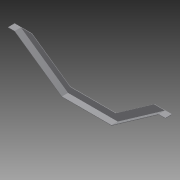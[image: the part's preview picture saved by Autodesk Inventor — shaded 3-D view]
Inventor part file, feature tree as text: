
AUTODESK INVENTOR PART (.ipt)
format: ipt  version: 2012 (Build 160160000, 160)  size: 97,280 bytes
history: native  units: in
note: dims shown in document units (in); Inventor stores cm internally (conversion verified against a paired STEP export)
features: extrude x2, sketch x1
ambient origin geometry x8: Origin, YZ Plane, XZ Plane, XY Plane, X Axis, Y Axis, Z Axis, Center Point
bodies: Solid1 (feature_tree)
feature tree (3):
  sketch  "Sketch1"  dims[d0=7.5in d1=0.9375in d2=0.9375in d3=0.9375in d4=0.9959in d5=0.9959in d6=8.704in d7=8.704in d8=5.0in d9=0.0625in d10=1.0in d11=0.0625in d12=1.0in d13=0.0625in d14=0.0625in d15=0.0in d16=1.0in d17=0.0in]
  extrude  "Extrusion1"  Depth=0.9375in
  extrude  "Extrusion2"  Depth=0.9375in
